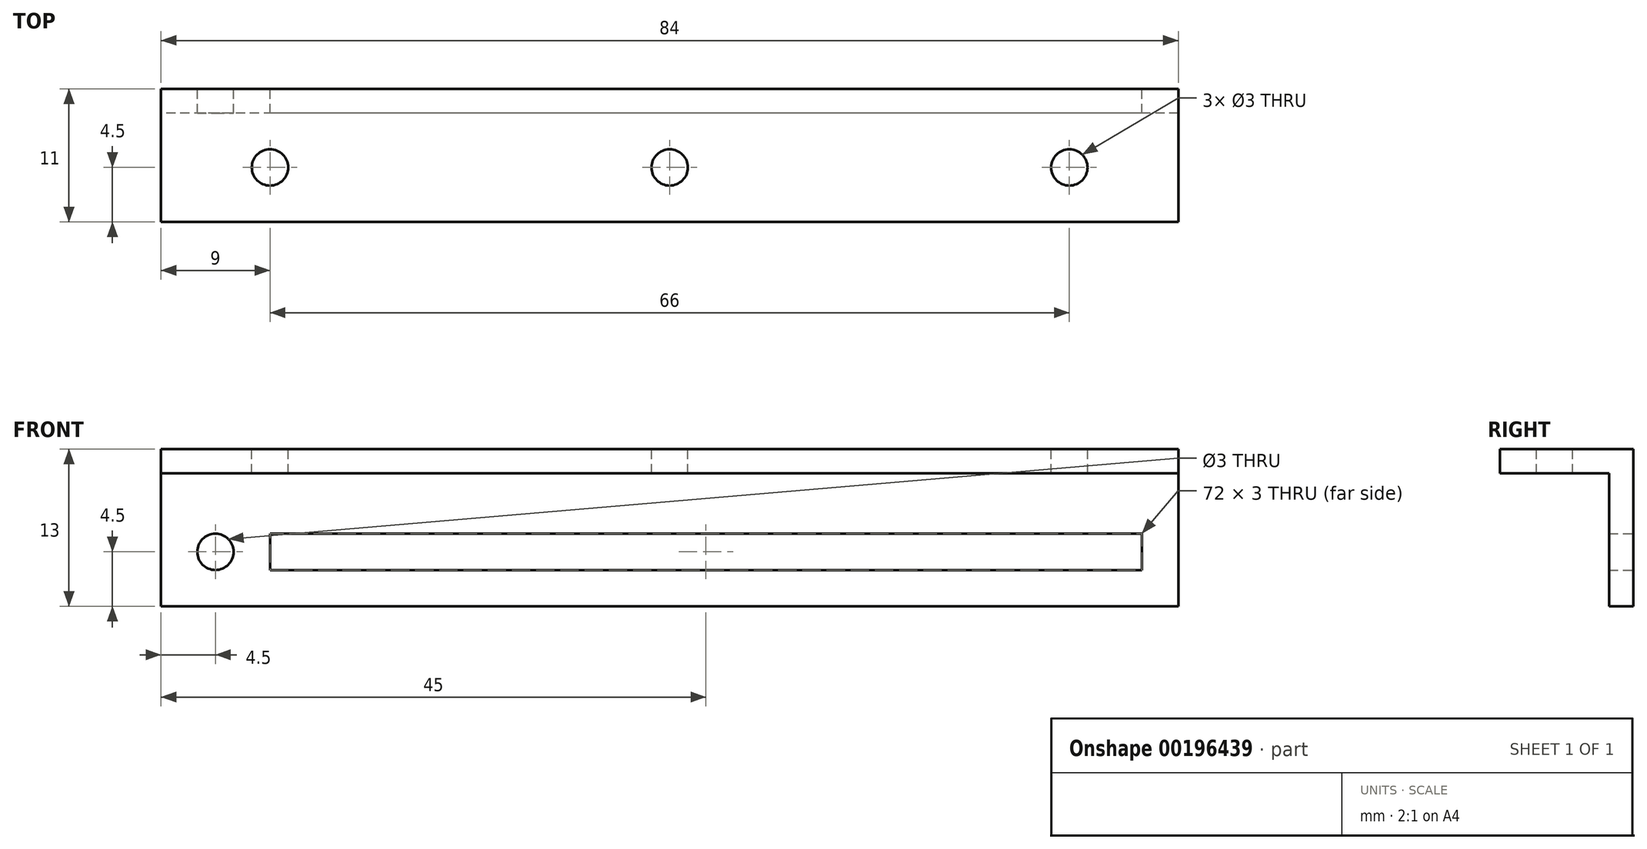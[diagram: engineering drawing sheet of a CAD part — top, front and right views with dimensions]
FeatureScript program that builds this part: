
annotation { "Feature Type Name" : "Feature", "Feature Type Description" : "" }
export const myFeature = defineFeature(function(context is Context, id is Id, definition is map)
    precondition{}
    {
        {
            var Q0;
            Q0=qCreatedBy(makeId("Front.planeOp"),FACE);
            var sketch = newSketch(context, id + "F0", { "sketchPlane" : qUnion([Q0])});
            skLineSegment(sketch, "E0.bottom", {"start": v(42, 4.5) * mm, "end": v(-42, 4.5) * mm});
            skLineSegment(sketch, "E0.top", {"start": v(42, -4.5) * mm, "end": v(-42, -4.5) * mm});
            skLineSegment(sketch, "E0.left", {"start": v(42, 4.5) * mm, "end": v(42, -4.5) * mm});
            skLineSegment(sketch, "E0.right", {"start": v(-42, 4.5) * mm, "end": v(-42, -4.5) * mm});
            skPoint(sketch, "E0.middle", {"position": v(0, 0) * mm});
            skLineSegment(sketch, "E1.bottom", {"start": v(39, 1.5) * mm, "end": v(-33, 1.5) * mm});
            skLineSegment(sketch, "E1.top", {"start": v(39, -1.5) * mm, "end": v(-33, -1.5) * mm});
            skLineSegment(sketch, "E1.left", {"start": v(39, 1.5) * mm, "end": v(39, -1.5) * mm});
            skLineSegment(sketch, "E1.right", {"start": v(-33, 1.5) * mm, "end": v(-33, -1.5) * mm});
            skCircle(sketch, "E2", {"center": v(-37.5, 0) * mm, "radius": 1.5 * mm});
            skLineSegment(sketch, "E3.top", {"start": v(42, 8.5) * mm, "end": v(-42, 8.5) * mm});
            skLineSegment(sketch, "E3.left", {"start": v(42, 4.5) * mm, "end": v(42, 8.5) * mm});
            skLineSegment(sketch, "E3.right", {"start": v(-42, 4.5) * mm, "end": v(-42, 8.5) * mm});
            skSolve(sketch);
        }
        {
            var Q0;
            Q0=qSketchRegion(id+"F0",true);
            extrude(context, id + "F1", {"entities" : qUnion([Q0]), "depth" : 2 * mm});
        }
        {
            var Q0;
            Q0=makeQuery(id+"F1.opExtrude","CAP_FACE",FACE,{"disambiguationData":[OSD([sQuery(id+"F0.wireOp",EDGE,"E0.top"),sQuery(id+"F0.wireOp",EDGE,"E0.left"),sQuery(id+"F0.wireOp",EDGE,"E0.right"),sQuery(id+"F0.wireOp",EDGE,"E1.bottom"),sQuery(id+"F0.wireOp",EDGE,"E1.top"),sQuery(id+"F0.wireOp",EDGE,"E1.left"),sQuery(id+"F0.wireOp",EDGE,"E1.right"),sQuery(id+"F0.wireOp",EDGE,"E2"),sQuery(id+"F0.wireOp",EDGE,"E3.top"),sQuery(id+"F0.wireOp",EDGE,"E3.left"),sQuery(id+"F0.wireOp",EDGE,"E3.right")])],"isStart":false});
            var sketch = newSketch(context, id + "F2", { "sketchPlane" : qUnion([Q0])});
            skLineSegment(sketch, "E4.bottom", {"start": v(42, 8.5) * mm, "end": v(-42, 8.5) * mm});
            skLineSegment(sketch, "E4.top", {"start": v(42, 6.5) * mm, "end": v(-42, 6.5) * mm});
            skLineSegment(sketch, "E4.left", {"start": v(42, 8.5) * mm, "end": v(42, 6.5) * mm});
            skLineSegment(sketch, "E4.right", {"start": v(-42, 8.5) * mm, "end": v(-42, 6.5) * mm});
            skSolve(sketch);
        }
        {
            var Q0;
            Q0 = qSketchRegion(id + "F2", true);
            extrude(context, id + "F3", {"entities" : qUnion([Q0]), "operationType" : NewBodyOperationType.ADD, "depth" : 9 * mm});
        }
        {
            var Q0;
            Q0=makeQuery(id+"F3.boolean.opBoolean","MERGE",FACE,{"derivedFrom":[makeQuery(id+"F1.opExtrude","SWEPT_FACE",FACE,{"disambiguationData":[OSD([sQuery(id+"F0.wireOp",EDGE,"E3.top")])]}),makeQuery(id+"F3.opExtrude","SWEPT_FACE",FACE,{"disambiguationData":[OSD([sQuery(id+"F2.wireOp",EDGE,"E4.bottom")])]})]});
            var sketch = newSketch(context, id + "F4", { "sketchPlane" : qUnion([Q0])});
            skCircle(sketch, "E5", {"center": v(0, -6.5) * mm, "radius": 1.5 * mm});
            skCircle(sketch, "E6", {"center": v(33, -6.5) * mm, "radius": 1.5 * mm});
            skCircle(sketch, "E7", {"center": v(-33, -6.5) * mm, "radius": 1.5 * mm});
            skSolve(sketch);
        }
        {
            var Q0;
            Q0 = qSketchRegion(id + "F4", true);
            extrude(context, id + "F5", {"entities" : qUnion([Q0]), "operationType" : NewBodyOperationType.REMOVE, "oppositeDirection" : true, "depth" : 25 * mm});
        }
    });
